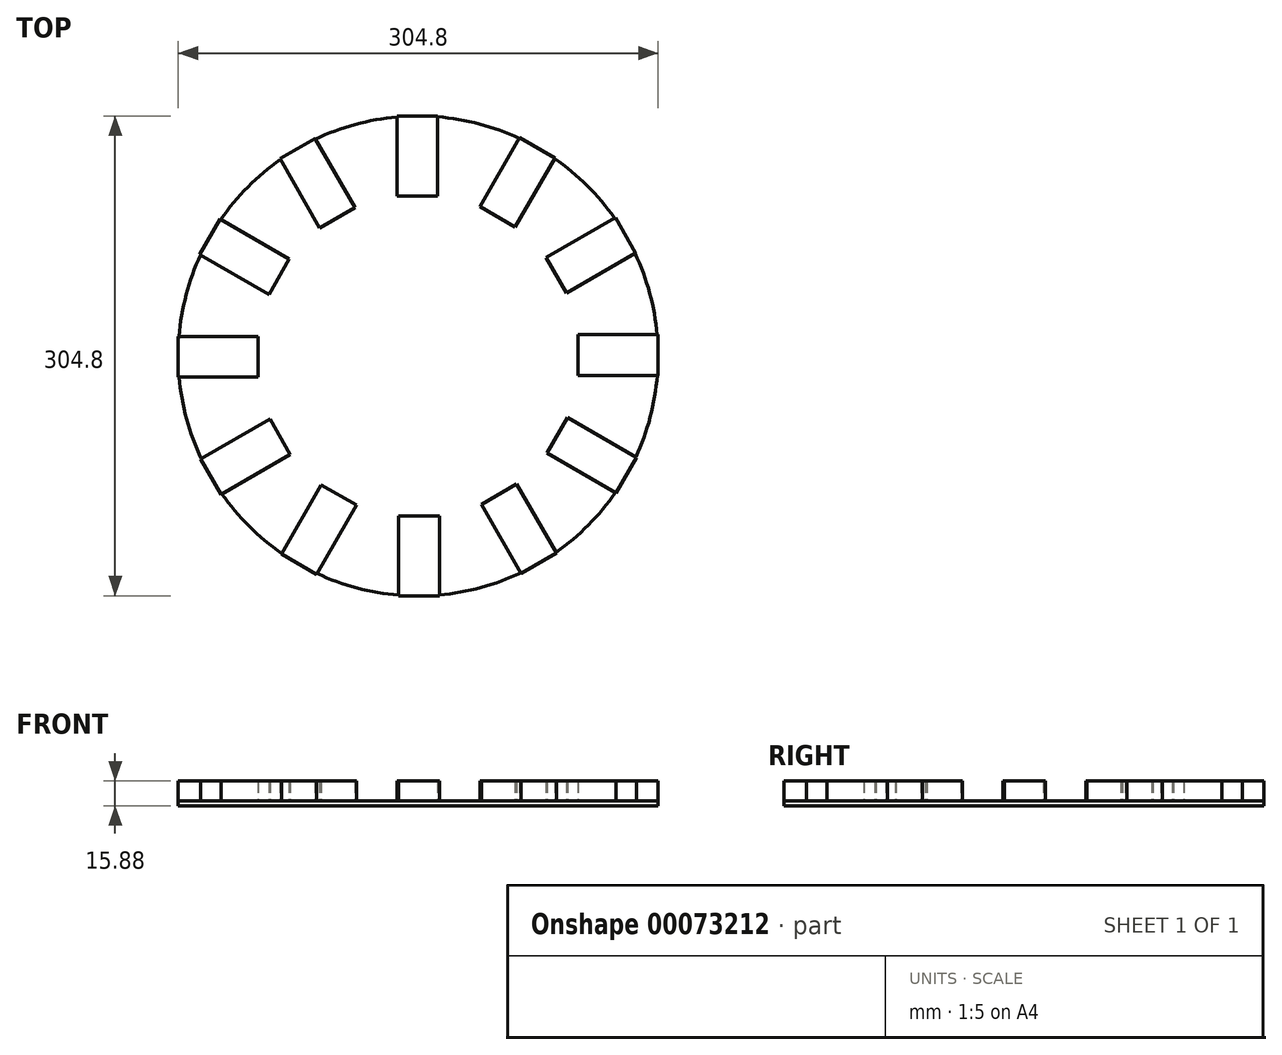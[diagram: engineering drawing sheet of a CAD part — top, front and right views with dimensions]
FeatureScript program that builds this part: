
annotation { "Feature Type Name" : "Feature", "Feature Type Description" : "" }
export const myFeature = defineFeature(function(context is Context, id is Id, definition is map)
    precondition{}
    {
        {
            var Q0;
            Q0=qCreatedBy(makeId("Top.planeOp"),FACE);
            var sketch = newSketch(context, id + "F0", { "sketchPlane" : qUnion([Q0])});
            skLineSegment(sketch, "E0.rect.bottom", {"start": v(12.37, 101.63) * mm, "end": v(-13.48, 101.63) * mm});
            skLineSegment(sketch, "E0.rect.top", {"start": v(12.37, 152.37) * mm, "end": v(-13.48, 152.37) * mm});
            skLineSegment(sketch, "E0.rect.left", {"start": v(12.37, 101.63) * mm, "end": v(12.37, 152.37) * mm});
            skLineSegment(sketch, "E0.rect.right", {"start": v(-13.48, 101.63) * mm, "end": v(-13.48, 152.37) * mm});
            skPoint(sketch, "E0.rect.middle", {"position": v(-0.55, 127) * mm});
            skPoint(sketch, "E0.rect.middle.positionSnap0", {"position": v(-12.94, 127) * mm});
            skPoint(sketch, "E0.rect.centerSnap0", {"position": v(-12.94, 127) * mm});
            skPoint(sketch, "E1.1.0", {"position": v(-63.98, 109.7) * mm});
            skPoint(sketch, "E1.1.1", {"position": v(-74.7, 103.51) * mm});
            skLineSegment(sketch, "E1.1.2", {"start": v(-65.47, 138.15) * mm, "end": v(-87.86, 125.22) * mm});
            skLineSegment(sketch, "E1.1.3", {"start": v(-40.1, 94.2) * mm, "end": v(-62.48, 81.27) * mm});
            skLineSegment(sketch, "E1.1.4", {"start": v(-40.1, 94.2) * mm, "end": v(-65.47, 138.15) * mm});
            skLineSegment(sketch, "E1.1.5", {"start": v(-62.48, 81.27) * mm, "end": v(-87.86, 125.22) * mm});
            skPoint(sketch, "E1.1.6", {"position": v(-74.7, 103.51) * mm});
            skPoint(sketch, "E1.2.0", {"position": v(-110.26, 63.02) * mm});
            skPoint(sketch, "E1.2.1", {"position": v(-116.46, 52.3) * mm});
            skLineSegment(sketch, "E1.2.2", {"start": v(-125.77, 86.9) * mm, "end": v(-138.7, 64.52) * mm});
            skLineSegment(sketch, "E1.2.3", {"start": v(-81.82, 61.53) * mm, "end": v(-94.75, 39.14) * mm});
            skLineSegment(sketch, "E1.2.4", {"start": v(-81.82, 61.53) * mm, "end": v(-125.77, 86.9) * mm});
            skLineSegment(sketch, "E1.2.5", {"start": v(-94.75, 39.14) * mm, "end": v(-138.7, 64.52) * mm});
            skPoint(sketch, "E1.2.6", {"position": v(-116.46, 52.3) * mm});
            skPoint(sketch, "E1.3.0", {"position": v(-127, -0.55) * mm});
            skPoint(sketch, "E1.3.1", {"position": v(-127, -12.94) * mm});
            skLineSegment(sketch, "E1.3.2", {"start": v(-152.37, 12.37) * mm, "end": v(-152.37, -13.48) * mm});
            skLineSegment(sketch, "E1.3.3", {"start": v(-101.63, 12.37) * mm, "end": v(-101.63, -13.48) * mm});
            skLineSegment(sketch, "E1.3.4", {"start": v(-101.63, 12.37) * mm, "end": v(-152.37, 12.37) * mm});
            skLineSegment(sketch, "E1.3.5", {"start": v(-101.63, -13.48) * mm, "end": v(-152.37, -13.48) * mm});
            skPoint(sketch, "E1.3.6", {"position": v(-127, -12.94) * mm});
            skPoint(sketch, "E1.4.0", {"position": v(-109.7, -63.98) * mm});
            skPoint(sketch, "E1.4.1", {"position": v(-103.51, -74.7) * mm});
            skLineSegment(sketch, "E1.4.2", {"start": v(-138.15, -65.47) * mm, "end": v(-125.22, -87.86) * mm});
            skLineSegment(sketch, "E1.4.3", {"start": v(-94.2, -40.1) * mm, "end": v(-81.27, -62.48) * mm});
            skLineSegment(sketch, "E1.4.4", {"start": v(-94.2, -40.1) * mm, "end": v(-138.15, -65.47) * mm});
            skLineSegment(sketch, "E1.4.5", {"start": v(-81.27, -62.48) * mm, "end": v(-125.22, -87.86) * mm});
            skPoint(sketch, "E1.4.6", {"position": v(-103.51, -74.7) * mm});
            skPoint(sketch, "E1.5.0", {"position": v(-63.02, -110.26) * mm});
            skPoint(sketch, "E1.5.1", {"position": v(-52.3, -116.46) * mm});
            skLineSegment(sketch, "E1.5.2", {"start": v(-86.9, -125.77) * mm, "end": v(-64.52, -138.7) * mm});
            skLineSegment(sketch, "E1.5.3", {"start": v(-61.53, -81.82) * mm, "end": v(-39.14, -94.75) * mm});
            skLineSegment(sketch, "E1.5.4", {"start": v(-61.53, -81.82) * mm, "end": v(-86.9, -125.77) * mm});
            skLineSegment(sketch, "E1.5.5", {"start": v(-39.14, -94.75) * mm, "end": v(-64.52, -138.7) * mm});
            skPoint(sketch, "E1.5.6", {"position": v(-52.3, -116.46) * mm});
            skPoint(sketch, "E1.6.0", {"position": v(0.55, -127) * mm});
            skPoint(sketch, "E1.6.1", {"position": v(12.94, -127) * mm});
            skLineSegment(sketch, "E1.6.2", {"start": v(-12.37, -152.37) * mm, "end": v(13.48, -152.37) * mm});
            skLineSegment(sketch, "E1.6.3", {"start": v(-12.37, -101.63) * mm, "end": v(13.48, -101.63) * mm});
            skLineSegment(sketch, "E1.6.4", {"start": v(-12.37, -101.63) * mm, "end": v(-12.37, -152.37) * mm});
            skLineSegment(sketch, "E1.6.5", {"start": v(13.48, -101.63) * mm, "end": v(13.48, -152.37) * mm});
            skPoint(sketch, "E1.6.6", {"position": v(12.94, -127) * mm});
            skPoint(sketch, "E1.7.0", {"position": v(63.98, -109.7) * mm});
            skPoint(sketch, "E1.7.1", {"position": v(74.7, -103.51) * mm});
            skLineSegment(sketch, "E1.7.2", {"start": v(65.47, -138.15) * mm, "end": v(87.86, -125.22) * mm});
            skLineSegment(sketch, "E1.7.3", {"start": v(40.1, -94.2) * mm, "end": v(62.48, -81.27) * mm});
            skLineSegment(sketch, "E1.7.4", {"start": v(40.1, -94.2) * mm, "end": v(65.47, -138.15) * mm});
            skLineSegment(sketch, "E1.7.5", {"start": v(62.48, -81.27) * mm, "end": v(87.86, -125.22) * mm});
            skPoint(sketch, "E1.7.6", {"position": v(74.7, -103.51) * mm});
            skPoint(sketch, "E1.8.0", {"position": v(110.26, -63.02) * mm});
            skPoint(sketch, "E1.8.1", {"position": v(116.46, -52.3) * mm});
            skLineSegment(sketch, "E1.8.2", {"start": v(125.77, -86.9) * mm, "end": v(138.7, -64.52) * mm});
            skLineSegment(sketch, "E1.8.3", {"start": v(81.82, -61.53) * mm, "end": v(94.75, -39.14) * mm});
            skLineSegment(sketch, "E1.8.4", {"start": v(81.82, -61.53) * mm, "end": v(125.77, -86.9) * mm});
            skLineSegment(sketch, "E1.8.5", {"start": v(94.75, -39.14) * mm, "end": v(138.7, -64.52) * mm});
            skPoint(sketch, "E1.8.6", {"position": v(116.46, -52.3) * mm});
            skPoint(sketch, "E1.9.0", {"position": v(127, 0.55) * mm});
            skPoint(sketch, "E1.9.1", {"position": v(127, 12.94) * mm});
            skLineSegment(sketch, "E1.9.2", {"start": v(152.37, -12.37) * mm, "end": v(152.37, 13.48) * mm});
            skLineSegment(sketch, "E1.9.3", {"start": v(101.63, -12.37) * mm, "end": v(101.63, 13.48) * mm});
            skLineSegment(sketch, "E1.9.4", {"start": v(101.63, -12.37) * mm, "end": v(152.37, -12.37) * mm});
            skLineSegment(sketch, "E1.9.5", {"start": v(101.63, 13.48) * mm, "end": v(152.37, 13.48) * mm});
            skPoint(sketch, "E1.9.6", {"position": v(127, 12.94) * mm});
            skPoint(sketch, "E1.10.0", {"position": v(109.7, 63.98) * mm});
            skPoint(sketch, "E1.10.1", {"position": v(103.51, 74.7) * mm});
            skLineSegment(sketch, "E1.10.2", {"start": v(138.15, 65.47) * mm, "end": v(125.22, 87.86) * mm});
            skLineSegment(sketch, "E1.10.3", {"start": v(94.2, 40.1) * mm, "end": v(81.27, 62.48) * mm});
            skLineSegment(sketch, "E1.10.4", {"start": v(94.2, 40.1) * mm, "end": v(138.15, 65.47) * mm});
            skLineSegment(sketch, "E1.10.5", {"start": v(81.27, 62.48) * mm, "end": v(125.22, 87.86) * mm});
            skPoint(sketch, "E1.10.6", {"position": v(103.51, 74.7) * mm});
            skPoint(sketch, "E1.11.0", {"position": v(63.02, 110.26) * mm});
            skPoint(sketch, "E1.11.1", {"position": v(52.3, 116.46) * mm});
            skLineSegment(sketch, "E1.11.2", {"start": v(86.9, 125.77) * mm, "end": v(64.52, 138.7) * mm});
            skLineSegment(sketch, "E1.11.3", {"start": v(61.53, 81.82) * mm, "end": v(39.14, 94.75) * mm});
            skLineSegment(sketch, "E1.11.4", {"start": v(61.53, 81.82) * mm, "end": v(86.9, 125.77) * mm});
            skLineSegment(sketch, "E1.11.5", {"start": v(39.14, 94.75) * mm, "end": v(64.52, 138.7) * mm});
            skPoint(sketch, "E1.11.6", {"position": v(52.3, 116.46) * mm});
            skSolve(sketch);
        }
        {
            var Q0;
            Q0 = qSketchRegion(id + "F0", true);
            extrude(context, id + "F1", {"entities" : qUnion([Q0]), "depth" : 12.7 * mm});
        }
        {
            var Q0;
            Q0=qCreatedBy(makeId("Top.planeOp"),FACE);
            var sketch = newSketch(context, id + "F2", { "sketchPlane" : qUnion([Q0])});
            skCircle(sketch, "E2", {"center": v(0, 0) * mm, "radius": 152.4 * mm});
            skSolve(sketch);
        }
        {
            var Q0;
            Q0=makeQuery(id+"F2.imprint","IMPRINT",FACE,{"disambiguationData":[TD([[makeQuery(id+"F2.imprint","IMPRINT",EDGE,{"derivedFrom":sQuery(id+"F2.wireOp",EDGE,"E2")}),1.0]])]});
            extrude(context, id + "F3", {"entities" : qUnion([Q0]), "operationType" : NewBodyOperationType.ADD, "oppositeDirection" : true, "depth" : 3.17 * mm});
        }
    });
